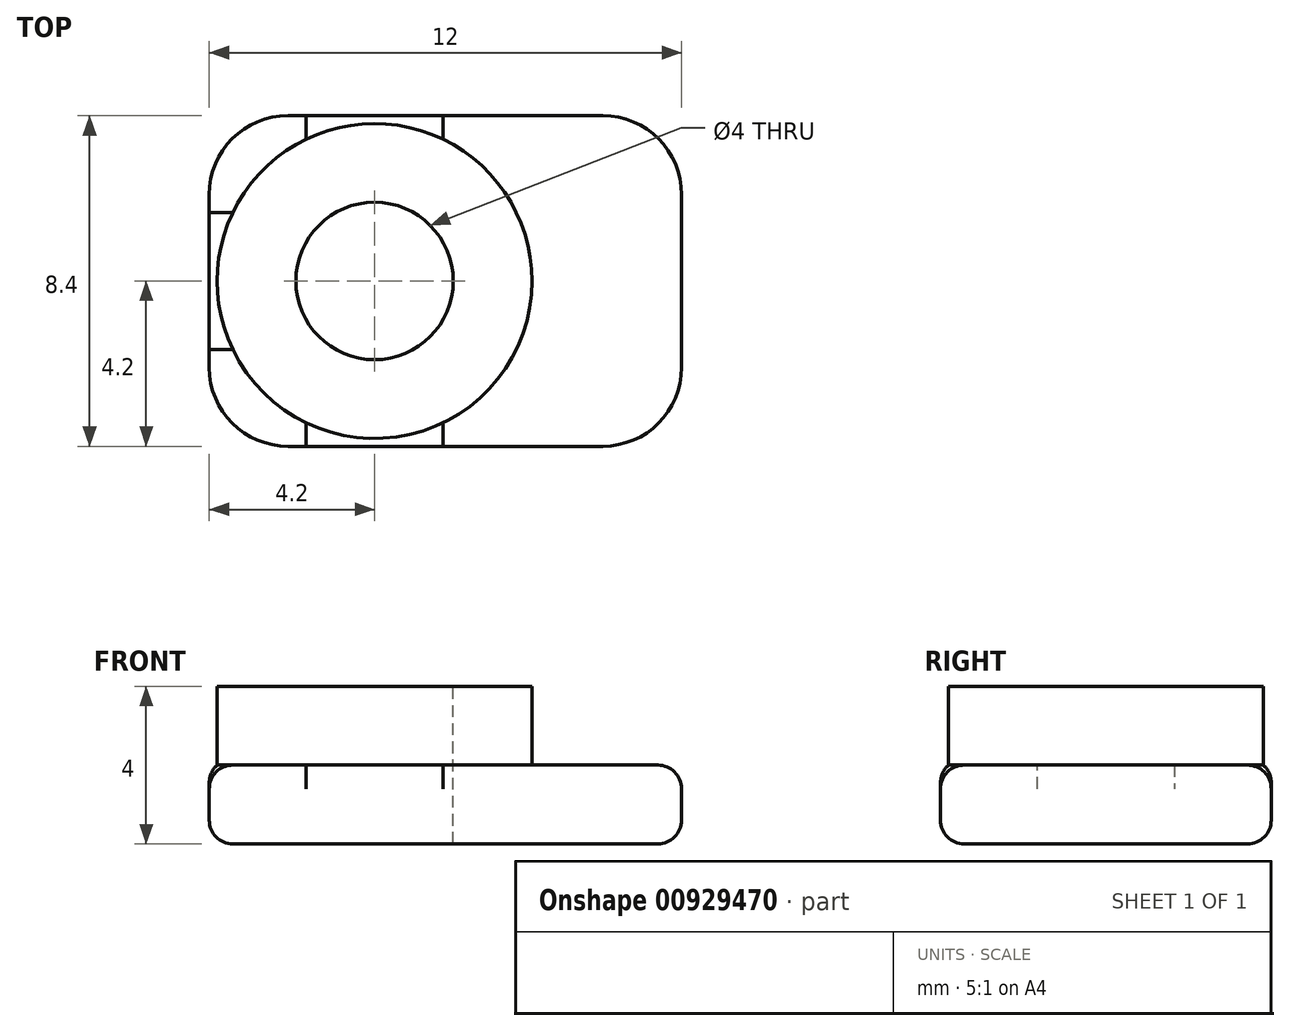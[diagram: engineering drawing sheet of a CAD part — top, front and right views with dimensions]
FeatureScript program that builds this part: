
annotation { "Feature Type Name" : "Feature", "Feature Type Description" : "" }
export const myFeature = defineFeature(function(context is Context, id is Id, definition is map)
    precondition{}
    {
        {
            var Q0;
            Q0=qCreatedBy(makeId("Top.planeOp"),FACE);
            var sketch = newSketch(context, id + "F0", { "sketchPlane" : qUnion([Q0])});
            skCircle(sketch, "E0", {"center": v(0, 0) * mm, "radius": 4 * mm});
            skSolve(sketch);
        }
        {
            var Q0;
            Q0 = qSketchRegion(id + "F0", true);
            extrude(context, id + "F1", {"entities" : qUnion([Q0]), "depth" : 2 * mm, "offsetDistance" : 25 * mm});
        }
        {
            var Q0;
            Q0=makeQuery(id+"F1.opExtrude","CAP_FACE",FACE,{"disambiguationData":[OSD([sQuery(id+"F0.wireOp",EDGE,"E0")])],"isStart":true});
            var sketch = newSketch(context, id + "F2", { "sketchPlane" : qUnion([Q0])});
            skLineSegment(sketch, "E1.bottom", {"start": v(-4.2, 4.2) * mm, "end": v(7.8, 4.2) * mm});
            skLineSegment(sketch, "E1.top", {"start": v(-4.2, -4.2) * mm, "end": v(7.8, -4.2) * mm});
            skLineSegment(sketch, "E1.left", {"start": v(-4.2, 4.2) * mm, "end": v(-4.2, -4.2) * mm});
            skLineSegment(sketch, "E1.right", {"start": v(7.8, 4.2) * mm, "end": v(7.8, -4.2) * mm});
            skSolve(sketch);
        }
        {
            var Q0;
            Q0 = qSketchRegion(id + "F2", true);
            extrude(context, id + "F3", {"entities" : qUnion([Q0]), "operationType" : NewBodyOperationType.ADD, "depth" : 2 * mm, "offsetDistance" : 25 * mm});
        }
        {
            var Q0;
            Q0=makeQuery(id+"F3.opExtrude","SWEPT_EDGE",EDGE,{"disambiguationData":[OSD([sQuery(id+"F2.wireOp",EDGE,"E1.top"),sQuery(id+"F2.wireOp",EDGE,"E1.left")])]});
            var Q1;
            Q1=makeQuery(id+"F3.opExtrude","SWEPT_EDGE",EDGE,{"disambiguationData":[OSD([sQuery(id+"F2.wireOp",EDGE,"E1.bottom"),sQuery(id+"F2.wireOp",EDGE,"E1.left")])]});
            var Q2;
            Q2=makeQuery(id+"F3.opExtrude","SWEPT_EDGE",EDGE,{"disambiguationData":[OSD([sQuery(id+"F2.wireOp",EDGE,"E1.top"),sQuery(id+"F2.wireOp",EDGE,"E1.right")])]});
            var Q3;
            Q3=makeQuery(id+"F3.opExtrude","SWEPT_EDGE",EDGE,{"disambiguationData":[OSD([sQuery(id+"F2.wireOp",EDGE,"E1.bottom"),sQuery(id+"F2.wireOp",EDGE,"E1.right")])]});
            fillet(context, id + "F4", {"entities" : qUnion([Q0, Q1, Q2, Q3]), "radius" : 2 * mm, "tangentPropagation" : true, "allowEdgeOverflow" : false});
        }
        {
            var Q0;
            Q0=makeQuery(id+"F3.opExtrude","CAP_EDGE",EDGE,{"disambiguationData":[OSD([sQuery(id+"F2.wireOp",EDGE,"E1.top")])],"isStart":true});
            var Q1;
            Q1=makeQuery(id+"F3.opExtrude","CAP_EDGE",EDGE,{"disambiguationData":[OSD([sQuery(id+"F2.wireOp",EDGE,"E1.bottom")])],"isStart":true});
            fillet(context, id + "F5", {"entities" : qUnion([Q0, Q1]), "radius" : .6 * mm, "tangentPropagation" : true, "allowEdgeOverflow" : false});
        }
        {
            var Q0;
            Q0=makeQuery(id+"F3.opExtrude","CAP_EDGE",EDGE,{"disambiguationData":[OSD([sQuery(id+"F2.wireOp",EDGE,"E1.bottom")])],"isStart":false});
            var Q1;
            Q1=makeQuery(id+"F3.opExtrude","CAP_EDGE",EDGE,{"disambiguationData":[OSD([sQuery(id+"F2.wireOp",EDGE,"E1.top")])],"isStart":false});
            var Q2;
            Q2=makeQuery(id+"F3.opExtrude","CAP_EDGE",EDGE,{"disambiguationData":[OSD([sQuery(id+"F2.wireOp",EDGE,"E1.left")])],"isStart":false});
            var Q3;
            Q3=makeQuery(id+"F3.opExtrude","CAP_EDGE",EDGE,{"disambiguationData":[OSD([sQuery(id+"F2.wireOp",EDGE,"E1.right")])],"isStart":false});
            fillet(context, id + "F6", {"entities" : qUnion([Q0, Q1, Q2, Q3]), "radius" : .6 * mm, "tangentPropagation" : true, "allowEdgeOverflow" : false});
        }
        {
            var Q0;
            Q0=makeQuery(id+"F1.opExtrude","CAP_FACE",FACE,{"disambiguationData":[OSD([sQuery(id+"F0.wireOp",EDGE,"E0")])],"isStart":false});
            var sketch = newSketch(context, id + "F7", { "sketchPlane" : qUnion([Q0])});
            skPoint(sketch, "E2", {"position": v(0, 0) * mm});
            skCircle(sketch, "E3", {"center": v(0, 0) * mm, "radius": 2 * mm});
            skSolve(sketch);
        }
        {
            var Q0;
            Q0 = qSketchRegion(id + "F7", true);
            var Q1;
            Q1=makeQuery(id+"F3.opExtrude","CAP_FACE",FACE,{"disambiguationData":[OSD([sQuery(id+"F2.wireOp",EDGE,"E1.bottom"),sQuery(id+"F2.wireOp",EDGE,"E1.top"),sQuery(id+"F2.wireOp",EDGE,"E1.left"),sQuery(id+"F2.wireOp",EDGE,"E1.right")])],"isStart":false});
            extrude(context, id + "F8", {"entities" : qUnion([Q0]), "operationType" : NewBodyOperationType.REMOVE, "endBound" : BoundingType.UP_TO_SURFACE, "oppositeDirection" : true, "depth" : 25 * mm, "endBoundEntityFace" : qUnion([Q1]), "offsetDistance" : 25 * mm});
        }
    });
